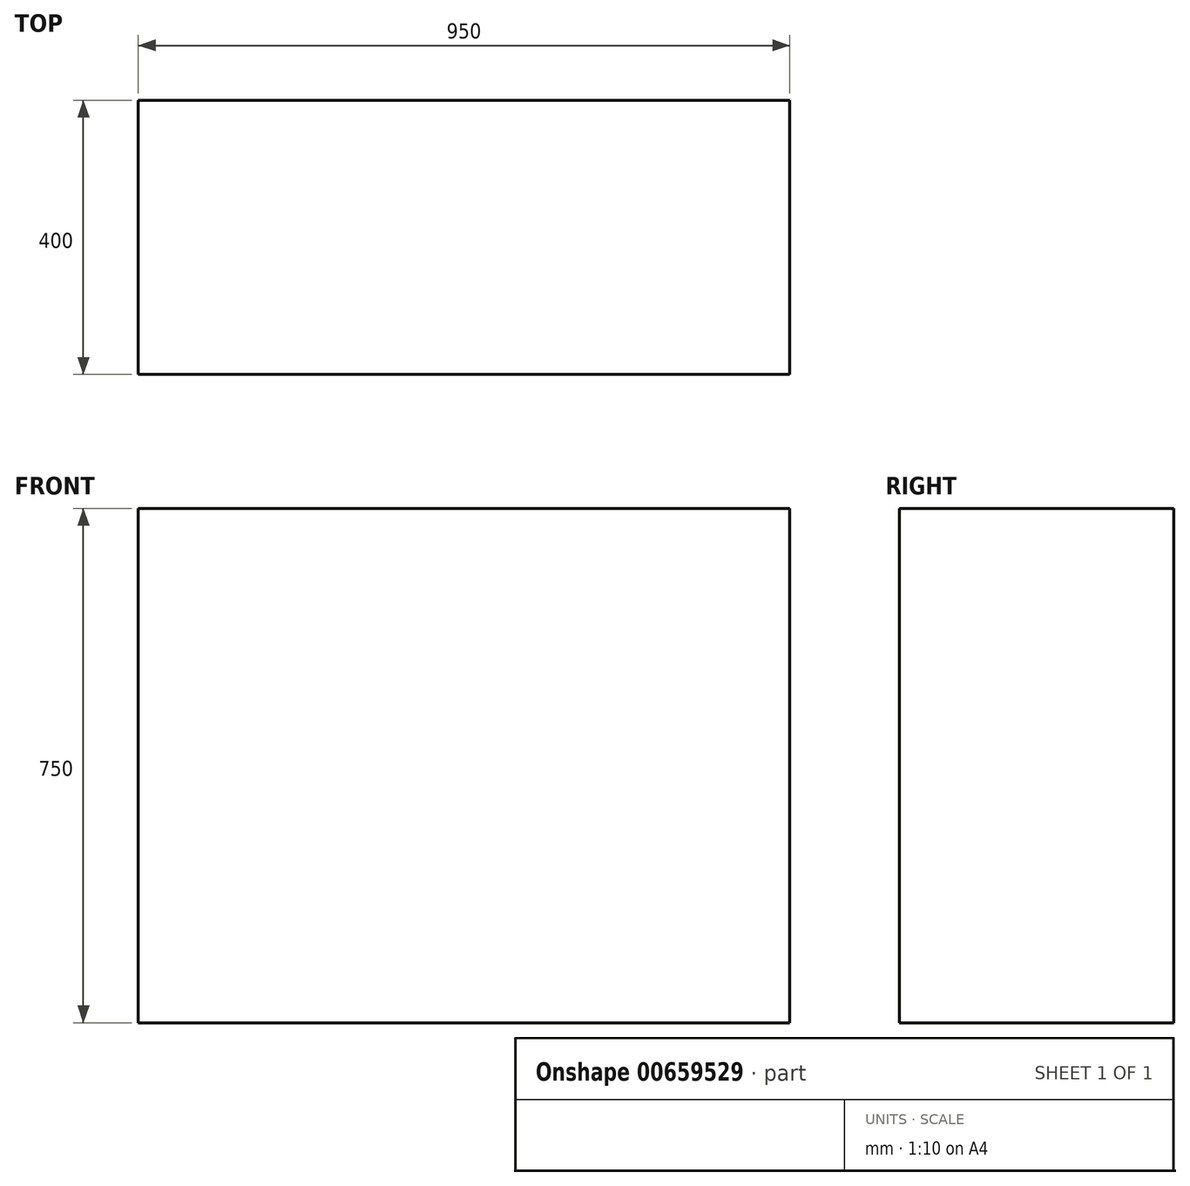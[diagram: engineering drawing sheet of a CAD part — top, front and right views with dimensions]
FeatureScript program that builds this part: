
annotation { "Feature Type Name" : "Feature", "Feature Type Description" : "" }
export const myFeature = defineFeature(function(context is Context, id is Id, definition is map)
    precondition{}
    {
        {
            var Q0;
            Q0=qCreatedBy(makeId("Top.planeOp"),FACE);
            var sketch = newSketch(context, id + "F0", { "sketchPlane" : qUnion([Q0])});
            skLineSegment(sketch, "E0.bottom", {"start": v(-467.22, 229.64) * mm, "end": v(482.78, 229.64) * mm});
            skLineSegment(sketch, "E0.top", {"start": v(-467.22, -170.36) * mm, "end": v(482.78, -170.36) * mm});
            skLineSegment(sketch, "E0.left", {"start": v(-467.22, 229.64) * mm, "end": v(-467.22, -170.36) * mm});
            skLineSegment(sketch, "E0.right", {"start": v(482.78, 229.64) * mm, "end": v(482.78, -170.36) * mm});
            skSolve(sketch);
        }
        {
            var Q0;
            Q0=makeQuery(id+"F0.imprint","IMPRINT",FACE,{"disambiguationData":[TD([[makeQuery(id+"F0.imprint","IMPRINT",EDGE,{"derivedFrom":sQuery(id+"F0.wireOp",EDGE,"E0.bottom")}),-1.0]])]});
            extrude(context, id + "F1", {"entities" : qUnion([Q0]), "depth" : 750 * mm, "offsetDistance" : 25 * mm});
        }
    });
